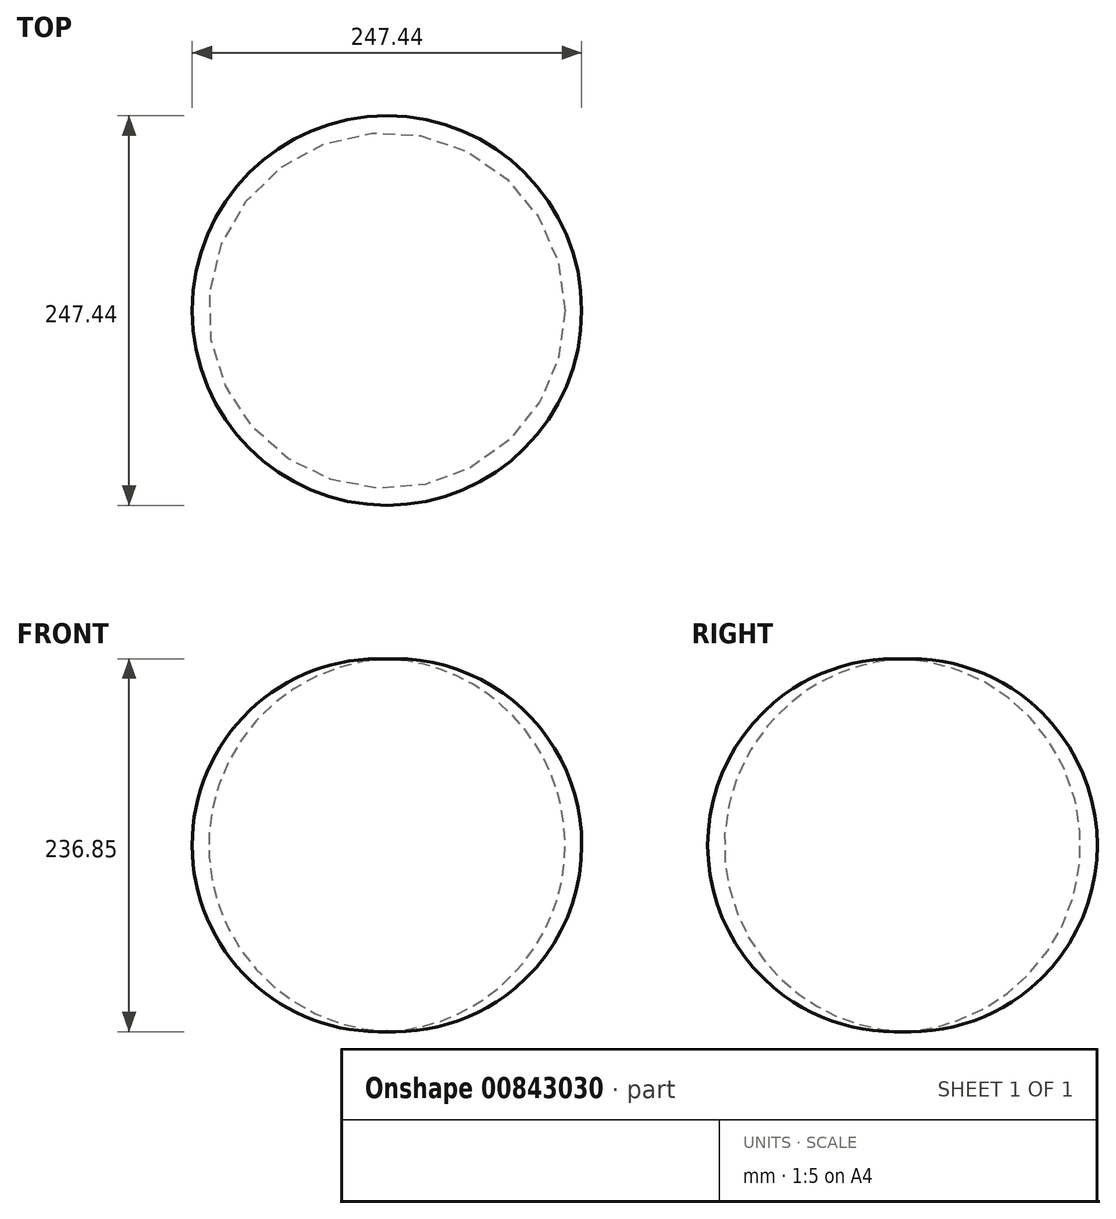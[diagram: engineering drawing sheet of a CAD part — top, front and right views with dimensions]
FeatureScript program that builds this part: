
annotation { "Feature Type Name" : "Feature", "Feature Type Description" : "" }
export const myFeature = defineFeature(function(context is Context, id is Id, definition is map)
    precondition{}
    {
        {
            var Q0;
            Q0=qCreatedBy(makeId("Front.planeOp"),FACE);
            var sketch = newSketch(context, id + "F0", { "sketchPlane" : qUnion([Q0])});
            skLineSegment(sketch, "E0", {"start": v(-205.22, 68.37) * mm, "end": v(-205.22, -168.24) * mm, "construction": true});
            skPoint(sketch, "E1", {"position": v(-205.22, -49.93) * mm});
            skArc(sketch, "E2", {"start": v(-205.22, -168.24) * mm, "mid": v(-81.5, -49.93) * mm, "end": v(-205.22, 68.37) * mm});
            skSolve(sketch);
        }
        {
            var Q0;
            Q0=sQuery(id+"F0.wireOp",EDGE,"E2");
            var Q1;
            Q1=sQuery(id+"F0.wireOp",EDGE,"E0");
            revolve(context, id + "F1", {"bodyType" : ToolBodyType.SURFACE, "surfaceOperationType" : NewSurfaceOperationType.NEW, "surfaceEntities" : qUnion([Q0]), "axis" : qUnion([Q1]), "revolveType" : RevolveType.FULL});
        }
        {
            var Q0;
            Q0=qCreatedBy(makeId("Top.planeOp"),FACE);
            cPlane(context, id + "F2", {"entities" : qUnion([Q0]), "cplaneType" : CPlaneType.OFFSET, "offset" : 50.8 * mm, "width" : 152.4 * mm, "height" : 152.4 * mm});
        }
        {
            var Q0;
            Q0=qCreatedBy(makeId("Top.planeOp"),FACE);
            cPlane(context, id + "F3", {"entities" : qUnion([Q0]), "cplaneType" : CPlaneType.OFFSET, "offset" : 25.4 * mm, "width" : 152.4 * mm, "height" : 152.4 * mm});
        }
        {
            var Q0;
            Q0=qCreatedBy(makeId("Top.planeOp"),FACE);
            cPlane(context, id + "F4", {"entities" : qUnion([Q0]), "cplaneType" : CPlaneType.OFFSET, "offset" : 25.4 * mm, "oppositeDirection" : true, "width" : 152.4 * mm, "height" : 152.4 * mm});
        }
        {
            var Q0;
            Q0=qCreatedBy(id+"F4.planeOp",FACE);
            cPlane(context, id + "F5", {"entities" : qUnion([Q0]), "cplaneType" : CPlaneType.OFFSET, "offset" : 25.4 * mm, "oppositeDirection" : true, "width" : 152.4 * mm, "height" : 152.4 * mm});
        }
        {
            var Q0;
            Q0=qCreatedBy(id+"F5.planeOp",FACE);
            cPlane(context, id + "F6", {"entities" : qUnion([Q0]), "cplaneType" : CPlaneType.OFFSET, "offset" : 25.4 * mm, "oppositeDirection" : true, "width" : 152.4 * mm, "height" : 152.4 * mm});
        }
    });
